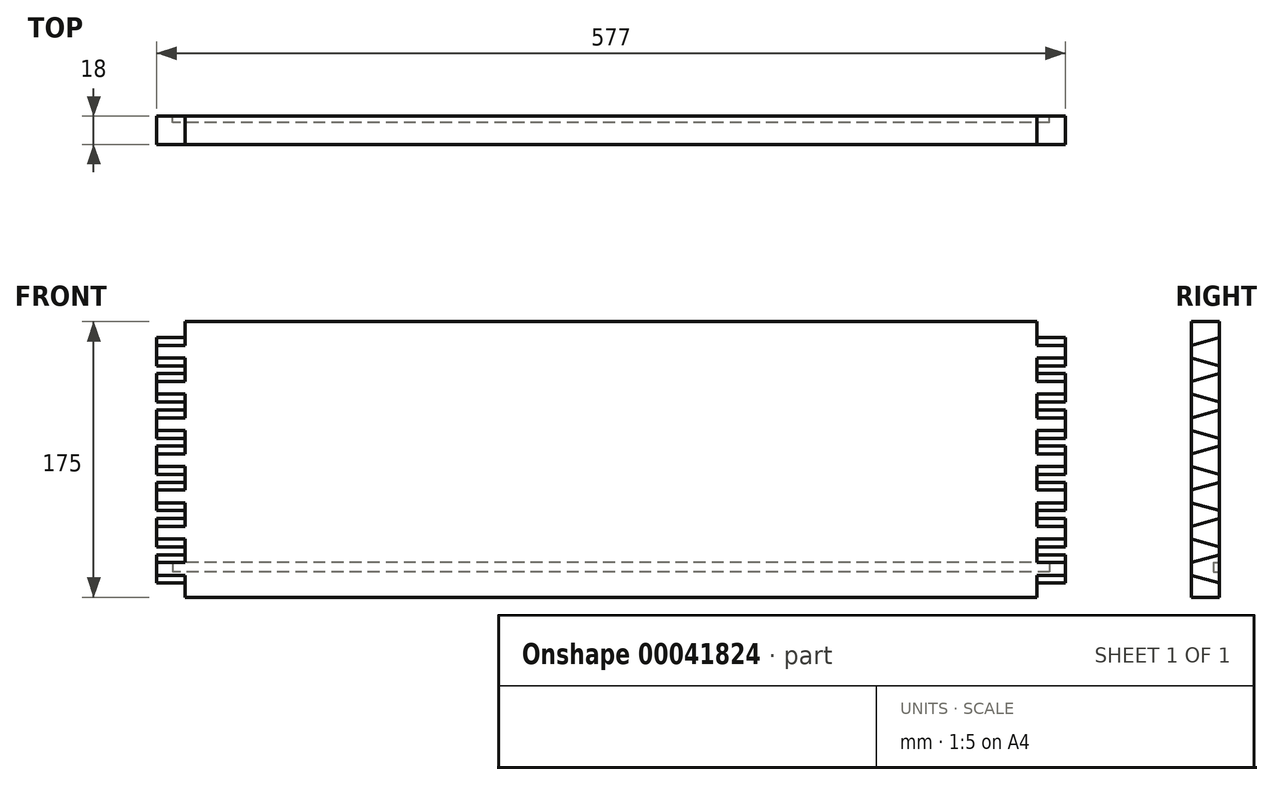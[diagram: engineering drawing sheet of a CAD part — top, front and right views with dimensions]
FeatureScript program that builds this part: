
annotation { "Feature Type Name" : "Feature", "Feature Type Description" : "" }
export const myFeature = defineFeature(function(context is Context, id is Id, definition is map)
    precondition{}
    {
        {
            var Q0;
            Q0=qCreatedBy(makeId("Front.planeOp"),FACE);
            var sketch = newSketch(context, id + "F0", { "sketchPlane" : qUnion([Q0])});
            skLineSegment(sketch, "E0.bottom", {"start": v(0, 0) * mm, "end": v(288.5, 0) * mm});
            skLineSegment(sketch, "E0.top", {"start": v(0, 175) * mm, "end": v(288.5, 175) * mm});
            skLineSegment(sketch, "E0.left", {"start": v(0, 0) * mm, "end": v(0, 175) * mm});
            skLineSegment(sketch, "E0.right", {"start": v(288.5, 0) * mm, "end": v(288.5, 175) * mm});
            skSolve(sketch);
        }
        {
            var Q0;
            Q0=makeQuery(id+"F0.imprint","IMPRINT",FACE,{"disambiguationData":[TD([[makeQuery(id+"F0.imprint","IMPRINT",EDGE,{"derivedFrom":sQuery(id+"F0.wireOp",EDGE,"E0.bottom")}),1.0]])]});
            extrude(context, id + "F1", {"entities" : qUnion([Q0]), "endBound" : BoundingType.SYMMETRIC, "depth" : 18 * mm});
        }
        {
            var Q0;
            Q0=makeQuery(id+"F1.opExtrude","SWEPT_FACE",FACE,{"disambiguationData":[OSD([sQuery(id+"F0.wireOp",EDGE,"E0.right")])]});
            var sketch = newSketch(context, id + "F2", { "sketchPlane" : qUnion([Q0])});
            skLineSegment(sketch, "E1", {"start": v(-9, 160) * mm, "end": v(-9, 152) * mm});
            skLineSegment(sketch, "E2", {"start": v(-9, 152) * mm, "end": v(9, 147) * mm});
            skLineSegment(sketch, "E3", {"start": v(9, 147) * mm, "end": v(9, 165) * mm});
            skLineSegment(sketch, "E4", {"start": v(9, 165) * mm, "end": v(-9, 160) * mm});
            skLineSegment(sketch, "E5.0.1.0", {"start": v(9, 124) * mm, "end": v(9, 142) * mm});
            skLineSegment(sketch, "E5.0.1.1", {"start": v(-9, 137) * mm, "end": v(-9, 129) * mm});
            skLineSegment(sketch, "E5.0.1.2", {"start": v(-9, 129) * mm, "end": v(9, 124) * mm});
            skLineSegment(sketch, "E5.0.1.3", {"start": v(9, 142) * mm, "end": v(-9, 137) * mm});
            skLineSegment(sketch, "E5.0.2.0", {"start": v(9, 101) * mm, "end": v(9, 119) * mm});
            skLineSegment(sketch, "E5.0.2.1", {"start": v(-9, 114) * mm, "end": v(-9, 106) * mm});
            skLineSegment(sketch, "E5.0.2.2", {"start": v(-9, 106) * mm, "end": v(9, 101) * mm});
            skLineSegment(sketch, "E5.0.2.3", {"start": v(9, 119) * mm, "end": v(-9, 114) * mm});
            skLineSegment(sketch, "E5.0.3.0", {"start": v(9, 78) * mm, "end": v(9, 96) * mm});
            skLineSegment(sketch, "E5.0.3.1", {"start": v(-9, 91) * mm, "end": v(-9, 83) * mm});
            skLineSegment(sketch, "E5.0.3.2", {"start": v(-9, 83) * mm, "end": v(9, 78) * mm});
            skLineSegment(sketch, "E5.0.3.3", {"start": v(9, 96) * mm, "end": v(-9, 91) * mm});
            skLineSegment(sketch, "E5.0.4.0", {"start": v(9, 55) * mm, "end": v(9, 73) * mm});
            skLineSegment(sketch, "E5.0.4.1", {"start": v(-9, 68) * mm, "end": v(-9, 60) * mm});
            skLineSegment(sketch, "E5.0.4.2", {"start": v(-9, 60) * mm, "end": v(9, 55) * mm});
            skLineSegment(sketch, "E5.0.4.3", {"start": v(9, 73) * mm, "end": v(-9, 68) * mm});
            skLineSegment(sketch, "E5.0.5.0", {"start": v(9, 32) * mm, "end": v(9, 50) * mm});
            skLineSegment(sketch, "E5.0.5.1", {"start": v(-9, 45) * mm, "end": v(-9, 37) * mm});
            skLineSegment(sketch, "E5.0.5.2", {"start": v(-9, 37) * mm, "end": v(9, 32) * mm});
            skLineSegment(sketch, "E5.0.5.3", {"start": v(9, 50) * mm, "end": v(-9, 45) * mm});
            skLineSegment(sketch, "E5.0.6.0", {"start": v(9, 9) * mm, "end": v(9, 27) * mm});
            skLineSegment(sketch, "E5.0.6.1", {"start": v(-9, 22) * mm, "end": v(-9, 14) * mm});
            skLineSegment(sketch, "E5.0.6.2", {"start": v(-9, 14) * mm, "end": v(9, 9) * mm});
            skLineSegment(sketch, "E5.0.6.3", {"start": v(9, 27) * mm, "end": v(-9, 22) * mm});
            skLineSegment(sketch, "E5.direction1", {"start": v(9, 147) * mm, "end": v(9, 147) * mm});
            skLineSegment(sketch, "E5.direction2", {"start": v(9, 147) * mm, "end": v(9, 124) * mm, "construction": true});
            skSolve(sketch);
        }
        {
            var Q0;
            {var subQ2=sQuery(id+"F2.wireOp",EDGE,"E4");Q0=makeQuery(id+"F2.imprint","IMPRINT",FACE,{"disambiguationData":[TD([[makeQuery(id+"F2.imprint","IMPRINT",EDGE,{"derivedFrom":subQ2}),-1.0]])]});}
            var Q1;
            {var subQ3=sQuery(id+"F2.wireOp",EDGE,"E2");Q1=makeQuery(id+"F2.imprint","IMPRINT",FACE,{"disambiguationData":[TD([[makeQuery(id+"F2.imprint","IMPRINT",EDGE,{"derivedFrom":subQ3}),-1.0]])]});}
            var Q2;
            {var subQ3=sQuery(id+"F2.wireOp",EDGE,"E5.0.2.2");Q2=makeQuery(id+"F2.imprint","IMPRINT",FACE,{"disambiguationData":[TD([[makeQuery(id+"F2.imprint","IMPRINT",EDGE,{"derivedFrom":subQ3}),-1.0]])]});}
            var Q3;
            {var subQ3=sQuery(id+"F2.wireOp",EDGE,"E5.0.3.2");Q3=makeQuery(id+"F2.imprint","IMPRINT",FACE,{"disambiguationData":[TD([[makeQuery(id+"F2.imprint","IMPRINT",EDGE,{"derivedFrom":subQ3}),-1.0]])]});}
            var Q4;
            {var subQ3=sQuery(id+"F2.wireOp",EDGE,"E5.0.4.2");Q4=makeQuery(id+"F2.imprint","IMPRINT",FACE,{"disambiguationData":[TD([[makeQuery(id+"F2.imprint","IMPRINT",EDGE,{"derivedFrom":subQ3}),-1.0]])]});}
            var Q5;
            {var subQ3=sQuery(id+"F2.wireOp",EDGE,"E5.0.5.2");Q5=makeQuery(id+"F2.imprint","IMPRINT",FACE,{"disambiguationData":[TD([[makeQuery(id+"F2.imprint","IMPRINT",EDGE,{"derivedFrom":subQ3}),-1.0]])]});}
            var Q6;
            {var subQ2=sQuery(id+"F2.wireOp",EDGE,"E5.0.6.2");Q6=makeQuery(id+"F2.imprint","IMPRINT",FACE,{"disambiguationData":[TD([[makeQuery(id+"F2.imprint","IMPRINT",EDGE,{"derivedFrom":subQ2}),-1.0]])]});}
            var Q7;
            {var subQ3=sQuery(id+"F2.wireOp",EDGE,"E5.0.1.2");Q7=makeQuery(id+"F2.imprint","IMPRINT",FACE,{"disambiguationData":[TD([[makeQuery(id+"F2.imprint","IMPRINT",EDGE,{"derivedFrom":subQ3}),-1.0]])]});}
            extrude(context, id + "F3", {"entities" : qUnion([Q0, Q1, Q2, Q3, Q4, Q5, Q6, Q7]), "operationType" : NewBodyOperationType.REMOVE, "oppositeDirection" : true, "depth" : 18 * mm});
        }
        {
            var Q0;
            Q0=makeQuery(id+"F1.opExtrude","SWEPT_BODY",BODY,{"disambiguationData":[OSD([sQuery(id+"F0.wireOp",EDGE,"E0.bottom"),sQuery(id+"F0.wireOp",EDGE,"E0.top"),sQuery(id+"F0.wireOp",EDGE,"E0.left"),sQuery(id+"F0.wireOp",EDGE,"E0.right")])]});
            var Q1;
            Q1=makeQuery(id+"F3.boolean.opBoolean","COPY",FACE,{"derivedFrom":makeQuery(id+"F3.opExtrude","CAP_FACE",FACE,{"disambiguationData":[OSD([sQuery(id+"F0.wireOp",EDGE,"E0.bottom"),sQuery(id+"F0.wireOp",EDGE,"E0.right"),sQuery(id+"F2.wireOp",EDGE,"E5.0.6.2")])],"isStart":false})});
            var Q2;
            Q2=makeQuery(id+"F3.boolean.opBoolean","COPY",FACE,{"derivedFrom":makeQuery(id+"F3.opExtrude","SWEPT_FACE",FACE,{"disambiguationData":[OSD([sQuery(id+"F2.wireOp",EDGE,"E5.0.6.2")])]})});
            var Q3;
            Q3=makeQuery(id+"F3.boolean.opBoolean","COPY",FACE,{"derivedFrom":makeQuery(id+"F3.opExtrude","CAP_FACE",FACE,{"disambiguationData":[OSD([sQuery(id+"F0.wireOp",EDGE,"E0.top"),sQuery(id+"F0.wireOp",EDGE,"E0.right"),sQuery(id+"F2.wireOp",EDGE,"E4")])],"isStart":false})});
            var Q4;
            Q4=makeQuery(id+"F3.boolean.opBoolean","COPY",FACE,{"derivedFrom":makeQuery(id+"F3.opExtrude","SWEPT_FACE",FACE,{"disambiguationData":[OSD([sQuery(id+"F2.wireOp",EDGE,"E4")])]})});
            var Q5;
            Q5=qCreatedBy(makeId("Right.planeOp"),FACE);
            mirror(context, id + "F4", {"operationType" : NewBodyOperationType.ADD, "entities" : qUnion([Q0]), "faces" : qUnion([Q1, Q2, Q3, Q4]), "mirrorPlane" : qUnion([Q5])});
        }
        {
            var Q0;
            {var subQ0=makeQuery(id+"F1.opExtrude","CAP_FACE",FACE,{"disambiguationData":[OSD([sQuery(id+"F0.wireOp",EDGE,"E0.bottom"),sQuery(id+"F0.wireOp",EDGE,"E0.top"),sQuery(id+"F0.wireOp",EDGE,"E0.left"),sQuery(id+"F0.wireOp",EDGE,"E0.right")])],"isStart":true});Q0=makeQuery(id+"F4.boolean.opBoolean","MERGE",FACE,{"derivedFrom":[subQ0,makeQuery(id+"F4.opPattern","COPY",FACE,{"derivedFrom":subQ0,"instanceName":"1"})]});}
            var sketch = newSketch(context, id + "F5", { "sketchPlane" : qUnion([Q0])});
            skLineSegment(sketch, "E6.bottom", {"start": v(-278.5, 22) * mm, "end": v(278.5, 22) * mm});
            skLineSegment(sketch, "E6.top", {"start": v(-278.5, 16) * mm, "end": v(278.5, 16) * mm});
            skLineSegment(sketch, "E6.left", {"start": v(-278.5, 22) * mm, "end": v(-278.5, 16) * mm});
            skLineSegment(sketch, "E6.right", {"start": v(278.5, 22) * mm, "end": v(278.5, 16) * mm});
            skSolve(sketch);
        }
        {
            var Q0;
            Q0=makeQuery(id+"F5.imprint","IMPRINT",FACE,{"disambiguationData":[TD([[makeQuery(id+"F5.imprint","IMPRINT",EDGE,{"derivedFrom":sQuery(id+"F5.wireOp",EDGE,"E6.bottom")}),-1.0]])]});
            extrude(context, id + "F6", {"entities" : qUnion([Q0]), "operationType" : NewBodyOperationType.REMOVE, "oppositeDirection" : true, "depth" : 4 * mm});
        }
    });
